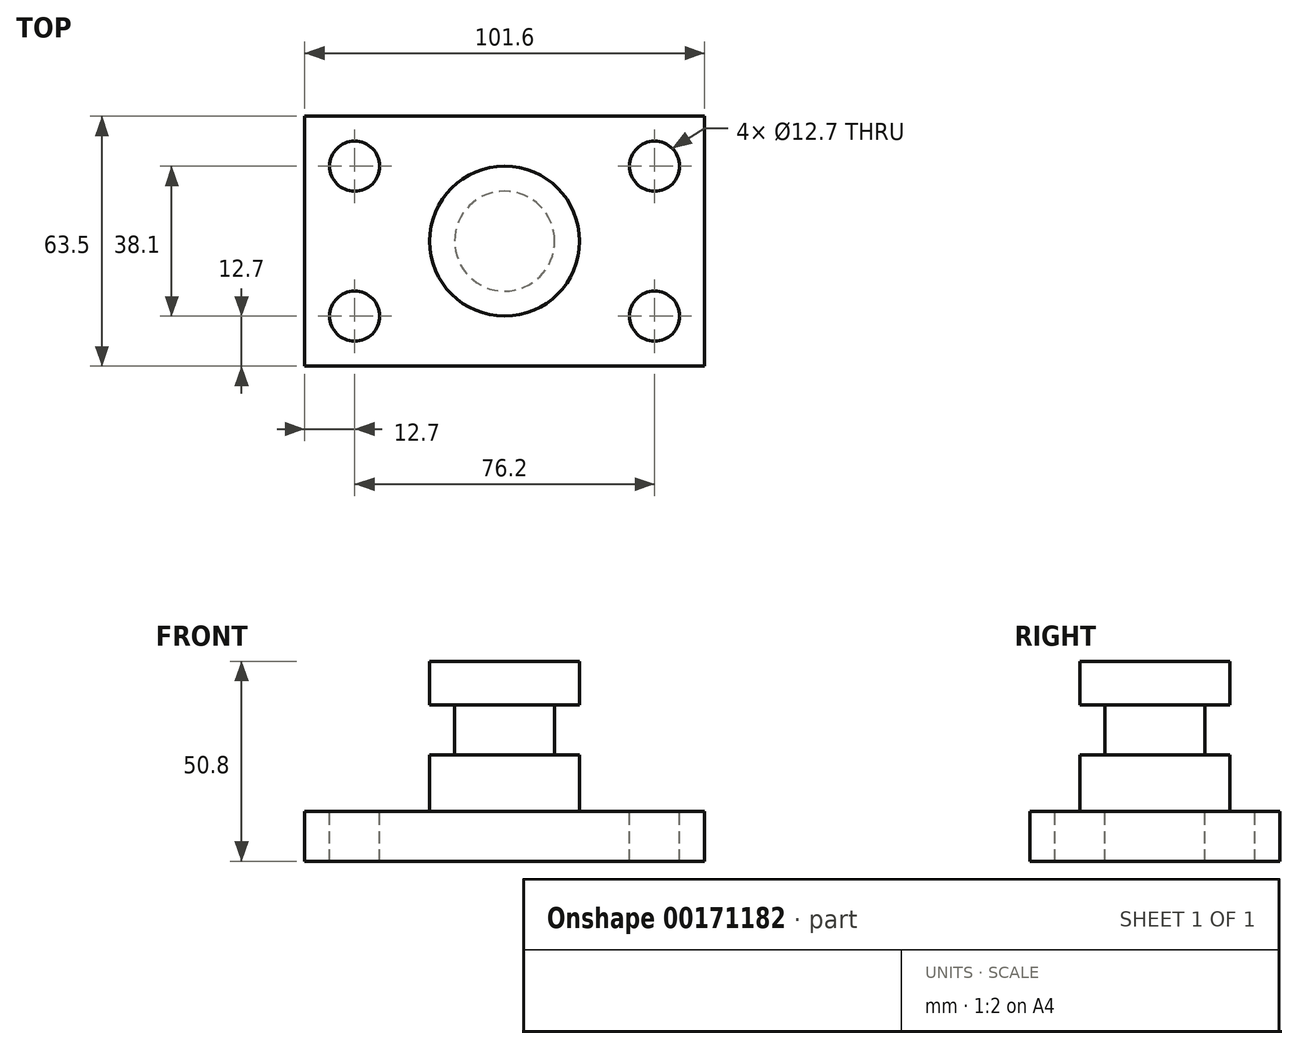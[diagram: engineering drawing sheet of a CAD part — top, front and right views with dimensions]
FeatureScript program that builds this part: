
annotation { "Feature Type Name" : "Feature", "Feature Type Description" : "" }
export const myFeature = defineFeature(function(context is Context, id is Id, definition is map)
    precondition{}
    {
        {
            var Q0;
            Q0=qCreatedBy(makeId("Top.planeOp"),FACE);
            var sketch = newSketch(context, id + "F0", { "sketchPlane" : qUnion([Q0])});
            skLineSegment(sketch, "E0.bottom", {"start": v(50.8, 31.75) * mm, "end": v(-50.8, 31.75) * mm});
            skLineSegment(sketch, "E0.top", {"start": v(50.8, -31.75) * mm, "end": v(-50.8, -31.75) * mm});
            skLineSegment(sketch, "E0.left", {"start": v(50.8, 31.75) * mm, "end": v(50.8, -31.75) * mm});
            skLineSegment(sketch, "E0.right", {"start": v(-50.8, 31.75) * mm, "end": v(-50.8, -31.75) * mm});
            skPoint(sketch, "E0.middle", {"position": v(0, 0) * mm});
            skSolve(sketch);
        }
        {
            var Q0;
            Q0=makeQuery(id+"F0.imprint","IMPRINT",FACE,{"disambiguationData":[TD([[makeQuery(id+"F0.imprint","IMPRINT",EDGE,{"derivedFrom":sQuery(id+"F0.wireOp",EDGE,"E0.bottom")}),1.0]])]});
            extrude(context, id + "F1", {"entities" : qUnion([Q0]), "depth" : 12.7 * mm});
        }
        {
            var Q0;
            Q0=makeQuery(id+"F1.opExtrude","CAP_FACE",FACE,{"disambiguationData":[OSD([sQuery(id+"F0.wireOp",EDGE,"E0.bottom"),sQuery(id+"F0.wireOp",EDGE,"E0.top"),sQuery(id+"F0.wireOp",EDGE,"E0.left"),sQuery(id+"F0.wireOp",EDGE,"E0.right")])],"isStart":false});
            var sketch = newSketch(context, id + "F2", { "sketchPlane" : qUnion([Q0])});
            skCircle(sketch, "E1", {"center": v(-38.1, 19.05) * mm, "radius": 6.35 * mm});
            skCircle(sketch, "E2", {"center": v(-38.1, -19.05) * mm, "radius": 6.35 * mm});
            skCircle(sketch, "E3", {"center": v(38.1, -19.05) * mm, "radius": 6.35 * mm});
            skCircle(sketch, "E4", {"center": v(38.1, 19.05) * mm, "radius": 6.35 * mm});
            skSolve(sketch);
        }
        {
            var Q0;
            Q0 = qSketchRegion(id + "F2", true);
            extrude(context, id + "F3", {"entities" : qUnion([Q0]), "operationType" : NewBodyOperationType.REMOVE, "oppositeDirection" : true, "depth" : 25.4 * mm});
        }
        {
            var Q0;
            Q0=qCreatedBy(makeId("Front.planeOp"),FACE);
            var sketch = newSketch(context, id + "F4", { "sketchPlane" : qUnion([Q0])});
            skLineSegment(sketch, "E5.bottom", {"start": v(0, 12.7) * mm, "end": v(-19.05, 12.7) * mm});
            skLineSegment(sketch, "E5.top", {"start": v(0, 50.8) * mm, "end": v(-19.05, 50.8) * mm});
            skLineSegment(sketch, "E5.left", {"start": v(0, 12.7) * mm, "end": v(0, 50.8) * mm});
            skLineSegment(sketch, "E5.right", {"start": v(-19.05, 12.7) * mm, "end": v(-19.05, 50.8) * mm});
            skPoint(sketch, "E5.middle", {"position": v(-9.53, 31.75) * mm});
            skSolve(sketch);
        }
        {
            var Q0;
            Q0=makeQuery(id+"F4.imprint","IMPRINT",FACE,{"disambiguationData":[TD([[makeQuery(id+"F4.imprint","IMPRINT",EDGE,{"derivedFrom":sQuery(id+"F4.wireOp",EDGE,"E5.bottom")}),-1.0]])]});
            var Q1;
            Q1=sQuery(id+"F4.wireOp",EDGE,"E5.left");
            revolve(context, id + "F5", {"operationType" : NewBodyOperationType.ADD, "entities" : qUnion([Q0]), "axis" : qUnion([Q1]), "revolveType" : RevolveType.FULL});
        }
        {
            var Q0;
            Q0=qCreatedBy(makeId("Front.planeOp"),FACE);
            var sketch = newSketch(context, id + "F6", { "sketchPlane" : qUnion([Q0])});
            skLineSegment(sketch, "E6.bottom", {"start": v(-25.4, 39.75) * mm, "end": v(-12.7, 39.75) * mm});
            skLineSegment(sketch, "E6.top", {"start": v(-25.4, 27.05) * mm, "end": v(-12.7, 27.05) * mm});
            skLineSegment(sketch, "E6.left", {"start": v(-25.4, 39.75) * mm, "end": v(-25.4, 27.05) * mm});
            skLineSegment(sketch, "E6.right", {"start": v(-12.7, 39.75) * mm, "end": v(-12.7, 27.05) * mm});
            skPoint(sketch, "E6.middle", {"position": v(-19.05, 33.4) * mm});
            skLineSegment(sketch, "E7", {"start": v(0, 70.77) * mm, "end": v(0, -28.75) * mm});
            skSolve(sketch);
        }
        {
            var Q0;
            Q0=makeQuery(id+"F6.imprint","IMPRINT",FACE,{"disambiguationData":[TD([[makeQuery(id+"F6.imprint","IMPRINT",EDGE,{"derivedFrom":sQuery(id+"F6.wireOp",EDGE,"E6.bottom")}),-1.0]])]});
            var Q1;
            Q1=sQuery(id+"F6.wireOp",EDGE,"E7");
            revolve(context, id + "F7", {"operationType" : NewBodyOperationType.REMOVE, "entities" : qUnion([Q0]), "axis" : qUnion([Q1]), "revolveType" : RevolveType.FULL, "oppositeDirection" : true});
        }
    });
